# Revit family: ВПВО_Eng
name_source: partatom
category: Mechanical Equipment
units: mm (PartAtom-declared; Revit-internal decimal feet)

## family parameters
Always vertical = Yes
Classification = None
Cut with Voids When Loaded = No
Part Type = Normal
Room Calculation Point = No
Round Connector Dimension = Use Diameter
Shared = No
Work Plane-Based = No

## types (159) — shared parameters
00_20_Manufacturer = Vents
00_20_Name = Medium pressure axial fan
Casing Material = Metal, painted, blue, matte RAL 5007
Frequency = 50 Hz
Load Classification = HVAC
Maintenance zone material = <By Category>
Manufacturer = Vents
Number of Fase = 3
URL = https://ventilation-system.com
Voltage = 400 V
t = 5 mm  [stored 0.0164042 ft]
zero-valued in all types: Default Elevation

## per-type parameters (varying)
| type | D2 | D3 | Diameter | Dn | Dvu | Dy | L | Ld | Length | Lk1 | Lk2 | Lk3 | Ly | Maximum Air Flow | Power | Rk | Rk1 | Rn1 | Weight | t1 |
| VPVO-400-2D/0,55-6/25/PAG | 490 mm | 390 mm  [stored 1.27953 ft] | 490 mm | 404 mm  [stored 1.32546 ft] | 390 mm  [stored 1.27953 ft] | 400 mm  [stored 1.31234 ft] | 350 mm  [stored 1.14829 ft] | 250 mm  [stored 0.82021 ft] | 350 mm  [stored 1.14829 ft] | 170 mm  [stored 0.557743 ft] | 300 mm | 235 mm  [stored 0.770997 ft] | 175 mm  [stored 0.574147 ft] | 5220.0 m³/h | 550 W | 200 mm  [stored 0.656168 ft] | 215 mm | 207 mm  [stored 0.679134 ft] | 23.4 kg | 345 mm  [stored 1.13189 ft] |
| VPVO-400-2D/0,75-6/30/PAG | 490 mm | 390 mm  [stored 1.27953 ft] | 490 mm | 404 mm  [stored 1.32546 ft] | 390 mm  [stored 1.27953 ft] | 400 mm  [stored 1.31234 ft] | 350 mm  [stored 1.14829 ft] | 250 mm  [stored 0.82021 ft] | 350 mm  [stored 1.14829 ft] | 170 mm  [stored 0.557743 ft] | 300 mm | 235 mm  [stored 0.770997 ft] | 175 mm  [stored 0.574147 ft] | 6120.0 m³/h | 750 W | 200 mm  [stored 0.656168 ft] | 215 mm | 207 mm  [stored 0.679134 ft] | 26.5 kg | 345 mm  [stored 1.13189 ft] |
| VPVO-400-2D/1,1-6/35/PAG | 490 mm | 390 mm  [stored 1.27953 ft] | 490 mm | 404 mm  [stored 1.32546 ft] | 390 mm  [stored 1.27953 ft] | 400 mm  [stored 1.31234 ft] | 450 mm | 350 mm  [stored 1.14829 ft] | 450 mm | 270 mm  [stored 0.885827 ft] | 400 mm  [stored 1.31234 ft] | 335 mm  [stored 1.09908 ft] | 225 mm  [stored 0.738189 ft] | 7200.0 m³/h | 1100 W | 200 mm  [stored 0.656168 ft] | 215 mm | 207 mm  [stored 0.679134 ft] | 27 kg | 445 mm  [stored 1.45997 ft] |
| VPVO-400-2D/1,5-6/40/PAG | 490 mm | 390 mm  [stored 1.27953 ft] | 490 mm | 404 mm  [stored 1.32546 ft] | 390 mm  [stored 1.27953 ft] | 400 mm  [stored 1.31234 ft] | 450 mm | 350 mm  [stored 1.14829 ft] | 450 mm | 270 mm  [stored 0.885827 ft] | 400 mm  [stored 1.31234 ft] | 335 mm  [stored 1.09908 ft] | 225 mm  [stored 0.738189 ft] | 7740.0 m³/h | 1500 W | 200 mm  [stored 0.656168 ft] | 215 mm | 207 mm  [stored 0.679134 ft] | 32.5 kg | 445 mm  [stored 1.45997 ft] |
| VPVO-400-2D/2,2-6/45/PAG | 490 mm | 390 mm  [stored 1.27953 ft] | 490 mm | 404 mm  [stored 1.32546 ft] | 390 mm  [stored 1.27953 ft] | 400 mm  [stored 1.31234 ft] | 450 mm | 350 mm  [stored 1.14829 ft] | 450 mm | 270 mm  [stored 0.885827 ft] | 400 mm  [stored 1.31234 ft] | 335 mm  [stored 1.09908 ft] | 225 mm  [stored 0.738189 ft] | 8460.0 m³/h | 2200 W | 200 mm  [stored 0.656168 ft] | 215 mm | 207 mm  [stored 0.679134 ft] | 34.5 kg | 445 mm  [stored 1.45997 ft] |
| VPVO-400-2D/2,2-8/45/PAG | 490 mm | 390 mm  [stored 1.27953 ft] | 490 mm | 404 mm  [stored 1.32546 ft] | 390 mm  [stored 1.27953 ft] | 400 mm  [stored 1.31234 ft] | 450 mm | 350 mm  [stored 1.14829 ft] | 450 mm | 270 mm  [stored 0.885827 ft] | 400 mm  [stored 1.31234 ft] | 335 mm  [stored 1.09908 ft] | 225 mm  [stored 0.738189 ft] | 8820.0 m³/h | 2200 W | 200 mm  [stored 0.656168 ft] | 215 mm | 207 mm  [stored 0.679134 ft] | 35 kg | 445 mm  [stored 1.45997 ft] |
| VPVO-400-4D/0,12-6/30/PAG | 490 mm | 390 mm  [stored 1.27953 ft] | 490 mm | 404 mm  [stored 1.32546 ft] | 390 mm  [stored 1.27953 ft] | 400 mm  [stored 1.31234 ft] | 350 mm  [stored 1.14829 ft] | 250 mm  [stored 0.82021 ft] | 350 mm  [stored 1.14829 ft] | 170 mm  [stored 0.557743 ft] | 300 mm | 235 mm  [stored 0.770997 ft] | 175 mm  [stored 0.574147 ft] | 3168.0 m³/h | 120 W | 200 mm  [stored 0.656168 ft] | 215 mm | 207 mm  [stored 0.679134 ft] | 19.5 kg | 345 mm  [stored 1.13189 ft] |
| VPVO-400-4D/0,18-6/35/PAG | 490 mm | 390 mm  [stored 1.27953 ft] | 490 mm | 404 mm  [stored 1.32546 ft] | 390 mm  [stored 1.27953 ft] | 400 mm  [stored 1.31234 ft] | 350 mm  [stored 1.14829 ft] | 250 mm  [stored 0.82021 ft] | 350 mm  [stored 1.14829 ft] | 170 mm  [stored 0.557743 ft] | 300 mm | 235 mm  [stored 0.770997 ft] | 175 mm  [stored 0.574147 ft] | 3600.0 m³/h | 180 W | 200 mm  [stored 0.656168 ft] | 215 mm | 207 mm  [stored 0.679134 ft] | 19.8 kg | 345 mm  [stored 1.13189 ft] |
| VPVO-400-4D/0,18-6/40/PAG | 490 mm | 390 mm  [stored 1.27953 ft] | 490 mm | 404 mm  [stored 1.32546 ft] | 390 mm  [stored 1.27953 ft] | 400 mm  [stored 1.31234 ft] | 350 mm  [stored 1.14829 ft] | 250 mm  [stored 0.82021 ft] | 350 mm  [stored 1.14829 ft] | 170 mm  [stored 0.557743 ft] | 300 mm | 235 mm  [stored 0.770997 ft] | 175 mm  [stored 0.574147 ft] | 3780.0 m³/h | 180 W | 200 mm  [stored 0.656168 ft] | 215 mm | 207 mm  [stored 0.679134 ft] | 19.8 kg | 345 mm  [stored 1.13189 ft] |
| VPVO-400-4D/0,25-6/45/PAG | 490 mm | 390 mm  [stored 1.27953 ft] | 490 mm | 404 mm  [stored 1.32546 ft] | 390 mm  [stored 1.27953 ft] | 400 mm  [stored 1.31234 ft] | 350 mm  [stored 1.14829 ft] | 250 mm  [stored 0.82021 ft] | 350 mm  [stored 1.14829 ft] | 170 mm  [stored 0.557743 ft] | 300 mm | 235 mm  [stored 0.770997 ft] | 175 mm  [stored 0.574147 ft] | 4248.0 m³/h | 250 W | 200 mm  [stored 0.656168 ft] | 215 mm | 207 mm  [stored 0.679134 ft] | 23.2 kg | 345 mm  [stored 1.13189 ft] |
| VPVO-400-4D/0,37-8/45/PAG | 490 mm | 390 mm  [stored 1.27953 ft] | 490 mm | 404 mm  [stored 1.32546 ft] | 390 mm  [stored 1.27953 ft] | 400 mm  [stored 1.31234 ft] | 350 mm  [stored 1.14829 ft] | 250 mm  [stored 0.82021 ft] | 350 mm  [stored 1.14829 ft] | 170 mm  [stored 0.557743 ft] | 300 mm | 235 mm  [stored 0.770997 ft] | 175 mm  [stored 0.574147 ft] | 4320.0 m³/h | 370 W | 200 mm  [stored 0.656168 ft] | 215 mm | 207 mm  [stored 0.679134 ft] | 23.9 kg | 345 mm  [stored 1.13189 ft] |
| VPVO-450-2D/0,75-6/25/PAG | 540 mm | 440 mm  [stored 1.44357 ft] | 540 mm | 454 mm | 440 mm  [stored 1.44357 ft] | 450 mm | 350 mm  [stored 1.14829 ft] | 250 mm  [stored 0.82021 ft] | 350 mm  [stored 1.14829 ft] | 170 mm  [stored 0.557743 ft] | 300 mm | 235 mm  [stored 0.770997 ft] | 175 mm  [stored 0.574147 ft] | 6750.0 m³/h | 750 W | 225 mm  [stored 0.738189 ft] | 240 mm  [stored 0.787402 ft] | 232 mm  [stored 0.761155 ft] | 36.1 kg | 345 mm  [stored 1.13189 ft] |
| VPVO-450-2D/1,1-6/30/PAG | 540 mm | 440 mm  [stored 1.44357 ft] | 540 mm | 454 mm | 440 mm  [stored 1.44357 ft] | 450 mm | 450 mm | 350 mm  [stored 1.14829 ft] | 450 mm | 270 mm  [stored 0.885827 ft] | 400 mm  [stored 1.31234 ft] | 335 mm  [stored 1.09908 ft] | 225 mm  [stored 0.738189 ft] | 8280.0 m³/h | 1100 W | 225 mm  [stored 0.738189 ft] | 240 mm  [stored 0.787402 ft] | 232 mm  [stored 0.761155 ft] | 36.6 kg | 445 mm  [stored 1.45997 ft] |
| VPVO-450-2D/1,5-6/35/PAG | 540 mm | 440 mm  [stored 1.44357 ft] | 540 mm | 454 mm | 440 mm  [stored 1.44357 ft] | 450 mm | 450 mm | 350 mm  [stored 1.14829 ft] | 450 mm | 270 mm  [stored 0.885827 ft] | 400 mm  [stored 1.31234 ft] | 335 mm  [stored 1.09908 ft] | 225 mm  [stored 0.738189 ft] | 9720.0 m³/h | 1500 W | 225 mm  [stored 0.738189 ft] | 240 mm  [stored 0.787402 ft] | 232 mm  [stored 0.761155 ft] | 42.1 kg | 445 mm  [stored 1.45997 ft] |
| VPVO-450-2D/2,2-6/40/PAG | 540 mm | 440 mm  [stored 1.44357 ft] | 540 mm | 454 mm | 440 mm  [stored 1.44357 ft] | 450 mm | 450 mm | 350 mm  [stored 1.14829 ft] | 450 mm | 270 mm  [stored 0.885827 ft] | 400 mm  [stored 1.31234 ft] | 335 mm  [stored 1.09908 ft] | 225 mm  [stored 0.738189 ft] | 10800.0 m³/h | 2200 W | 225 mm  [stored 0.738189 ft] | 240 mm  [stored 0.787402 ft] | 232 mm  [stored 0.761155 ft] | 44.1 kg | 445 mm  [stored 1.45997 ft] |
| VPVO-450-2D/3-8/40/PAG | 540 mm | 440 mm  [stored 1.44357 ft] | 540 mm | 454 mm | 440 mm  [stored 1.44357 ft] | 450 mm | 450 mm | 350 mm  [stored 1.14829 ft] | 450 mm | 270 mm  [stored 0.885827 ft] | 400 mm  [stored 1.31234 ft] | 335 mm  [stored 1.09908 ft] | 225 mm  [stored 0.738189 ft] | 11250.0 m³/h | 3000 W | 225 mm  [stored 0.738189 ft] | 240 mm  [stored 0.787402 ft] | 232 mm  [stored 0.761155 ft] | 53.6 kg | 445 mm  [stored 1.45997 ft] |
| VPVO-450-2D/4-8/45/PAG | 540 mm | 440 mm  [stored 1.44357 ft] | 540 mm | 454 mm | 440 mm  [stored 1.44357 ft] | 450 mm | 550 mm | 450 mm | 550 mm | 370 mm  [stored 1.21391 ft] | 500 mm | 435 mm  [stored 1.42717 ft] | 275 mm | 12600.0 m³/h | 4000 W | 225 mm  [stored 0.738189 ft] | 240 mm  [stored 0.787402 ft] | 232 mm  [stored 0.761155 ft] | 63.7 kg | 545 mm |
| VPVO-450-4D/0,12-6/25/PAG | 540 mm | 440 mm  [stored 1.44357 ft] | 540 mm | 454 mm | 440 mm  [stored 1.44357 ft] | 450 mm | 350 mm  [stored 1.14829 ft] | 250 mm  [stored 0.82021 ft] | 350 mm  [stored 1.14829 ft] | 170 mm  [stored 0.557743 ft] | 300 mm | 235 mm  [stored 0.770997 ft] | 175 mm  [stored 0.574147 ft] | 3420.0 m³/h | 120 W | 225 mm  [stored 0.738189 ft] | 240 mm  [stored 0.787402 ft] | 232 mm  [stored 0.761155 ft] | 29.1 kg | 345 mm  [stored 1.13189 ft] |
| VPVO-450-4D/0,18-6/30/PAG | 540 mm | 440 mm  [stored 1.44357 ft] | 540 mm | 454 mm | 440 mm  [stored 1.44357 ft] | 450 mm | 350 mm  [stored 1.14829 ft] | 250 mm  [stored 0.82021 ft] | 350 mm  [stored 1.14829 ft] | 170 mm  [stored 0.557743 ft] | 300 mm | 235 mm  [stored 0.770997 ft] | 175 mm  [stored 0.574147 ft] | 3960.0 m³/h | 180 W | 225 mm  [stored 0.738189 ft] | 240 mm  [stored 0.787402 ft] | 232 mm  [stored 0.761155 ft] | 29.4 kg | 345 mm  [stored 1.13189 ft] |
| VPVO-450-4D/0,25-6/35/PAG | 540 mm | 440 mm  [stored 1.44357 ft] | 540 mm | 454 mm | 440 mm  [stored 1.44357 ft] | 450 mm | 350 mm  [stored 1.14829 ft] | 250 mm  [stored 0.82021 ft] | 350 mm  [stored 1.14829 ft] | 170 mm  [stored 0.557743 ft] | 300 mm | 235 mm  [stored 0.770997 ft] | 175 mm  [stored 0.574147 ft] | 4860.0 m³/h | 250 W | 225 mm  [stored 0.738189 ft] | 240 mm  [stored 0.787402 ft] | 232 mm  [stored 0.761155 ft] | 32.8 kg | 345 mm  [stored 1.13189 ft] |
| VPVO-450-4D/0,25-6/40/PAG | 540 mm | 440 mm  [stored 1.44357 ft] | 540 mm | 454 mm | 440 mm  [stored 1.44357 ft] | 450 mm | 350 mm  [stored 1.14829 ft] | 250 mm  [stored 0.82021 ft] | 350 mm  [stored 1.14829 ft] | 170 mm  [stored 0.557743 ft] | 300 mm | 235 mm  [stored 0.770997 ft] | 175 mm  [stored 0.574147 ft] | 5220.0 m³/h | 250 W | 225 mm  [stored 0.738189 ft] | 240 mm  [stored 0.787402 ft] | 232 mm  [stored 0.761155 ft] | 32.8 kg | 345 mm  [stored 1.13189 ft] |
| VPVO-450-4D/0,37-6/45/PAG | 540 mm | 440 mm  [stored 1.44357 ft] | 540 mm | 454 mm | 440 mm  [stored 1.44357 ft] | 450 mm | 350 mm  [stored 1.14829 ft] | 250 mm  [stored 0.82021 ft] | 350 mm  [stored 1.14829 ft] | 170 mm  [stored 0.557743 ft] | 300 mm | 235 mm  [stored 0.770997 ft] | 175 mm  [stored 0.574147 ft] | 5760.0 m³/h | 370 W | 225 mm  [stored 0.738189 ft] | 240 mm  [stored 0.787402 ft] | 232 mm  [stored 0.761155 ft] | 33 kg | 345 mm  [stored 1.13189 ft] |
| VPVO-450-4D/0,55-8/45/PAG | 540 mm | 440 mm  [stored 1.44357 ft] | 540 mm | 454 mm | 440 mm  [stored 1.44357 ft] | 450 mm | 350 mm  [stored 1.14829 ft] | 250 mm  [stored 0.82021 ft] | 350 mm  [stored 1.14829 ft] | 170 mm  [stored 0.557743 ft] | 300 mm | 235 mm  [stored 0.770997 ft] | 175 mm  [stored 0.574147 ft] | 6120.0 m³/h | 550 W | 225 mm  [stored 0.738189 ft] | 240 mm  [stored 0.787402 ft] | 232 mm  [stored 0.761155 ft] | 36.6 kg | 345 mm  [stored 1.13189 ft] |
| VPVO-500-2D/1,1-6/25/PAG | 600 mm | 490 mm | 600 mm | 504 mm | 490 mm | 500 mm | 450 mm | 350 mm  [stored 1.14829 ft] | 450 mm | 270 mm  [stored 0.885827 ft] | 400 mm  [stored 1.31234 ft] | 335 mm  [stored 1.09908 ft] | 225 mm  [stored 0.738189 ft] | 8460.0 m³/h | 1100 W | 250 mm  [stored 0.82021 ft] | 265 mm  [stored 0.869423 ft] | 257 mm  [stored 0.843176 ft] | 48.2 kg | 445 mm  [stored 1.45997 ft] |
| VPVO-560-2D/1,5-6/25/PAG | 660 mm | 550 mm | 660 mm | 564 mm | 550 mm | 560 mm | 450 mm | 350 mm  [stored 1.14829 ft] | 450 mm | 270 mm  [stored 0.885827 ft] | 400 mm  [stored 1.31234 ft] | 335 mm  [stored 1.09908 ft] | 225 mm  [stored 0.738189 ft] | 10440.0 m³/h | 1500 W | 280 mm  [stored 0.918635 ft] | 295 mm  [stored 0.967848 ft] | 287 mm | 70.8 kg | 445 mm  [stored 1.45997 ft] |
| VPVO-630-2D/3-8/25/PAG | 730 mm | 620 mm | 730 mm | 634 mm | 620 mm | 630 mm | 450 mm | 350 mm  [stored 1.14829 ft] | 450 mm | 270 mm  [stored 0.885827 ft] | 400 mm  [stored 1.31234 ft] | 335 mm  [stored 1.09908 ft] | 225 mm  [stored 0.738189 ft] | 13680.0 m³/h | 3000 W | 315 mm  [stored 1.03346 ft] | 330 mm  [stored 1.08268 ft] | 322 mm  [stored 1.05643 ft] | 88 kg | 445 mm  [stored 1.45997 ft] |
| VPVO-710-2D/7,5-6/20/PAG | 810 mm | 700 mm | 810 mm | 714 mm | 700 mm | 710 mm | 550 mm | 450 mm | 550 mm | 370 mm  [stored 1.21391 ft] | 500 mm | 435 mm  [stored 1.42717 ft] | 275 mm | 22680.0 m³/h | 7500 W | 355 mm | 370 mm  [stored 1.21391 ft] | 362 mm  [stored 1.18766 ft] | 150.8 kg | 545 mm |
| VPVO-800-4D/1,1-6/20/PAG | 900 mm | 790 mm | 900 mm | 804 mm | 790 mm | 800 mm | 450 mm | 350 mm  [stored 1.14829 ft] | 450 mm | 270 mm  [stored 0.885827 ft] | 400 mm  [stored 1.31234 ft] | 335 mm  [stored 1.09908 ft] | 225 mm  [stored 0.738189 ft] | 15120.0 m³/h | 1100 W | 400 mm  [stored 1.31234 ft] | 415 mm  [stored 1.36155 ft] | 407 mm  [stored 1.3353 ft] | 115.6 kg | 445 mm  [stored 1.45997 ft] |
| VPVO-900-4D/3-8/20/PAG | 1015 mm | 890 mm | 1015 mm | 904 mm | 890 mm | 900 mm | 550 mm | 450 mm | 550 mm | 370 mm  [stored 1.21391 ft] | 500 mm | 435 mm  [stored 1.42717 ft] | 275 mm | 21600.0 m³/h | 3000 W | 450 mm | 465 mm | 457 mm | 134.8 kg | 545 mm |
| VPVO-1000-4D/5,5-8/25/PAG | 1115 mm | 990 mm | 1115 mm | 1004 mm | 990 mm | 1000 mm | 550 mm | 450 mm | 550 mm | 370 mm  [stored 1.21391 ft] | 500 mm | 435 mm  [stored 1.42717 ft] | 275 mm | 30960.0 m³/h | 5500 W | 500 mm | 515 mm | 507 mm | 200.5 kg | 545 mm |
| VPVO-1120-4D/7,5-8/25/PAG | 1270 mm | 1110 mm | 1270 mm | 1124 mm | 1110 mm | 1120 mm | 650 mm | 550 mm | 650 mm | 470 mm | 600 mm | 535 mm | 325 mm  [stored 1.06627 ft] | 43920.0 m³/h | 7500 W | 560 mm | 575 mm | 567 mm | 222 kg | 645 mm |
| VPVO-1250-4D/7,5-8/25/PAG | 1400 mm | 1240 mm | 1400 mm | 1254 mm | 1240 mm | 1250 mm | 650 mm | 550 mm | 650 mm | 470 mm | 600 mm | 535 mm | 325 mm  [stored 1.06627 ft] | 45000.0 m³/h | 7500 W | 625 mm | 640 mm | 632 mm | 241 kg | 645 mm |
| VPVO-500-2D/1,5-6/30/PAG | 600 mm | 490 mm | 600 mm | 504 mm | 490 mm | 500 mm | 450 mm | 350 mm  [stored 1.14829 ft] | 450 mm | 270 mm  [stored 0.885827 ft] | 400 mm  [stored 1.31234 ft] | 335 mm  [stored 1.09908 ft] | 225 mm  [stored 0.738189 ft] | 10440.0 m³/h | 1500 W | 250 mm  [stored 0.82021 ft] | 265 mm  [stored 0.869423 ft] | 257 mm  [stored 0.843176 ft] | 53.7 kg | 445 mm  [stored 1.45997 ft] |
| VPVO-500-2D/2,2-6/35/PAG | 600 mm | 490 mm | 600 mm | 504 mm | 490 mm | 500 mm | 450 mm | 350 mm  [stored 1.14829 ft] | 450 mm | 270 mm  [stored 0.885827 ft] | 400 mm  [stored 1.31234 ft] | 335 mm  [stored 1.09908 ft] | 225 mm  [stored 0.738189 ft] | 12240.0 m³/h | 2200 W | 250 mm  [stored 0.82021 ft] | 265 mm  [stored 0.869423 ft] | 257 mm  [stored 0.843176 ft] | 55.7 kg | 445 mm  [stored 1.45997 ft] |
| VPVO-500-2D/3-8/35/PAG | 600 mm | 490 mm | 600 mm | 504 mm | 490 mm | 500 mm | 450 mm | 350 mm  [stored 1.14829 ft] | 450 mm | 270 mm  [stored 0.885827 ft] | 400 mm  [stored 1.31234 ft] | 335 mm  [stored 1.09908 ft] | 225 mm  [stored 0.738189 ft] | 13320.0 m³/h | 3000 W | 250 mm  [stored 0.82021 ft] | 265 mm  [stored 0.869423 ft] | 257 mm  [stored 0.843176 ft] | 65.3 kg | 445 mm  [stored 1.45997 ft] |
| VPVO-500-2D/4-8/40/PAG | 600 mm | 490 mm | 600 mm | 504 mm | 490 mm | 500 mm | 550 mm | 450 mm | 550 mm | 370 mm  [stored 1.21391 ft] | 500 mm | 435 mm  [stored 1.42717 ft] | 275 mm | 15120.0 m³/h | 4000 W | 250 mm  [stored 0.82021 ft] | 265 mm  [stored 0.869423 ft] | 257 mm  [stored 0.843176 ft] | 75.4 kg | 545 mm |
| VPVO-500-2D/5,5-8/45/PAG | 600 mm | 490 mm | 600 mm | 504 mm | 490 mm | 500 mm | 550 mm | 450 mm | 550 mm | 370 mm  [stored 1.21391 ft] | 500 mm | 435 mm  [stored 1.42717 ft] | 275 mm | 16200.0 m³/h | 5500 W | 250 mm  [stored 0.82021 ft] | 265 mm  [stored 0.869423 ft] | 257 mm  [stored 0.843176 ft] | 96.8 kg | 545 mm |
| VPVO-500-4D/0,18-6/25/PAG | 600 mm | 490 mm | 600 mm | 504 mm | 490 mm | 500 mm | 350 mm  [stored 1.14829 ft] | 250 mm  [stored 0.82021 ft] | 350 mm  [stored 1.14829 ft] | 170 mm  [stored 0.557743 ft] | 300 mm | 235 mm  [stored 0.770997 ft] | 175 mm  [stored 0.574147 ft] | 4320.0 m³/h | 180 W | 250 mm  [stored 0.82021 ft] | 265 mm  [stored 0.869423 ft] | 257 mm  [stored 0.843176 ft] | 61.5 kg | 345 mm  [stored 1.13189 ft] |
| VPVO-500-4D/0,25-6/30/PAG | 600 mm | 490 mm | 600 mm | 504 mm | 490 mm | 500 mm | 350 mm  [stored 1.14829 ft] | 250 mm  [stored 0.82021 ft] | 350 mm  [stored 1.14829 ft] | 170 mm  [stored 0.557743 ft] | 300 mm | 235 mm  [stored 0.770997 ft] | 175 mm  [stored 0.574147 ft] | 5256.0 m³/h | 250 W | 250 mm  [stored 0.82021 ft] | 265 mm  [stored 0.869423 ft] | 257 mm  [stored 0.843176 ft] | 61.7 kg | 345 mm  [stored 1.13189 ft] |
| VPVO-500-4D/0,37-6/35/PAG | 600 mm | 490 mm | 600 mm | 504 mm | 490 mm | 500 mm | 350 mm  [stored 1.14829 ft] | 250 mm  [stored 0.82021 ft] | 350 mm  [stored 1.14829 ft] | 170 mm  [stored 0.557743 ft] | 300 mm | 235 mm  [stored 0.770997 ft] | 175 mm  [stored 0.574147 ft] | 6120.0 m³/h | 370 W | 250 mm  [stored 0.82021 ft] | 265 mm  [stored 0.869423 ft] | 257 mm  [stored 0.843176 ft] | 64.8 kg | 345 mm  [stored 1.13189 ft] |
| VPVO-500-4D/0,37-6/40/PAG | 600 mm | 490 mm | 600 mm | 504 mm | 490 mm | 500 mm | 350 mm  [stored 1.14829 ft] | 250 mm  [stored 0.82021 ft] | 350 mm  [stored 1.14829 ft] | 170 mm  [stored 0.557743 ft] | 300 mm | 235 mm  [stored 0.770997 ft] | 175 mm  [stored 0.574147 ft] | 6480.0 m³/h | 370 W | 250 mm  [stored 0.82021 ft] | 265 mm  [stored 0.869423 ft] | 257 mm  [stored 0.843176 ft] | 64.8 kg | 345 mm  [stored 1.13189 ft] |
| VPVO-500-4D/0,55-6/45/PAG | 600 mm | 490 mm | 600 mm | 504 mm | 490 mm | 500 mm | 450 mm | 350 mm  [stored 1.14829 ft] | 450 mm | 270 mm  [stored 0.885827 ft] | 400 mm  [stored 1.31234 ft] | 335 mm  [stored 1.09908 ft] | 225 mm  [stored 0.738189 ft] | 7560.0 m³/h | 550 W | 250 mm  [stored 0.82021 ft] | 265 mm  [stored 0.869423 ft] | 257 mm  [stored 0.843176 ft] | 65.6 kg | 445 mm  [stored 1.45997 ft] |
| VPVO-500-4D/0,75-8/45/PAG | 600 mm | 490 mm | 600 mm | 504 mm | 490 mm | 500 mm | 450 mm | 350 mm  [stored 1.14829 ft] | 450 mm | 270 mm  [stored 0.885827 ft] | 400 mm  [stored 1.31234 ft] | 335 mm  [stored 1.09908 ft] | 225 mm  [stored 0.738189 ft] | 8280.0 m³/h | 750 W | 250 mm  [stored 0.82021 ft] | 265 mm  [stored 0.869423 ft] | 257 mm  [stored 0.843176 ft] | 71.4 kg | 445 mm  [stored 1.45997 ft] |
| VPVO-560-2D/2,2/6/30/PAG | 660 mm | 550 mm | 660 mm | 564 mm | 550 mm | 560 mm | 450 mm | 350 mm  [stored 1.14829 ft] | 450 mm | 270 mm  [stored 0.885827 ft] | 400 mm  [stored 1.31234 ft] | 335 mm  [stored 1.09908 ft] | 225 mm  [stored 0.738189 ft] | 12600.0 m³/h | 2200 W | 280 mm  [stored 0.918635 ft] | 295 mm  [stored 0.967848 ft] | 287 mm | 72.8 kg | 445 mm  [stored 1.45997 ft] |
| VPVO-560-2D/3-8/30/PAG | 660 mm | 550 mm | 660 mm | 564 mm | 550 mm | 560 mm | 450 mm | 350 mm  [stored 1.14829 ft] | 450 mm | 270 mm  [stored 0.885827 ft] | 400 mm  [stored 1.31234 ft] | 335 mm  [stored 1.09908 ft] | 225 mm  [stored 0.738189 ft] | 14040.0 m³/h | 3000 W | 280 mm  [stored 0.918635 ft] | 295 mm  [stored 0.967848 ft] | 287 mm | 82.4 kg | 445 mm  [stored 1.45997 ft] |
| VPVO-560-2D/4-8/35/PAG | 660 mm | 550 mm | 660 mm | 564 mm | 550 mm | 560 mm | 550 mm | 450 mm | 550 mm | 370 mm  [stored 1.21391 ft] | 500 mm | 435 mm  [stored 1.42717 ft] | 275 mm | 17280.0 m³/h | 4000 W | 280 mm  [stored 0.918635 ft] | 295 mm  [stored 0.967848 ft] | 287 mm | 92.5 kg | 545 mm |
| VPVO-560-2D/5,5-8/40/PAG | 660 mm | 550 mm | 660 mm | 564 mm | 550 mm | 560 mm | 550 mm | 450 mm | 550 mm | 370 mm  [stored 1.21391 ft] | 500 mm | 435 mm  [stored 1.42717 ft] | 275 mm | 18540.0 m³/h | 5500 W | 280 mm  [stored 0.918635 ft] | 295 mm  [stored 0.967848 ft] | 287 mm | 113.9 kg | 545 mm |
| VPVO-560-2D/7,5-8/45/PAG | 660 mm | 550 mm | 660 mm | 564 mm | 550 mm | 560 mm | 550 mm | 450 mm | 550 mm | 370 mm  [stored 1.21391 ft] | 500 mm | 435 mm  [stored 1.42717 ft] | 275 mm | 21600.0 m³/h | 7500 W | 280 mm  [stored 0.918635 ft] | 295 mm  [stored 0.967848 ft] | 287 mm | 117.9 kg | 545 mm |
| VPVO-560-4D/0,25-6/25/PAG | 660 mm | 550 mm | 660 mm | 564 mm | 550 mm | 560 mm | 350 mm  [stored 1.14829 ft] | 250 mm  [stored 0.82021 ft] | 350 mm  [stored 1.14829 ft] | 170 mm  [stored 0.557743 ft] | 300 mm | 235 mm  [stored 0.770997 ft] | 175 mm  [stored 0.574147 ft] | 5040.0 m³/h | 250 W | 280 mm  [stored 0.918635 ft] | 295 mm  [stored 0.967848 ft] | 287 mm | 61.5 kg | 345 mm  [stored 1.13189 ft] |
| VPVO-560-4D/0,37-6/30/PAG | 660 mm | 550 mm | 660 mm | 564 mm | 550 mm | 560 mm | 350 mm  [stored 1.14829 ft] | 250 mm  [stored 0.82021 ft] | 350 mm  [stored 1.14829 ft] | 170 mm  [stored 0.557743 ft] | 300 mm | 235 mm  [stored 0.770997 ft] | 175 mm  [stored 0.574147 ft] | 6480.0 m³/h | 370 W | 280 mm  [stored 0.918635 ft] | 295 mm  [stored 0.967848 ft] | 287 mm | 61.7 kg | 345 mm  [stored 1.13189 ft] |
| VPVO-560-4D/0,55-6/35/PAG | 660 mm | 550 mm | 660 mm | 564 mm | 550 mm | 560 mm | 350 mm  [stored 1.14829 ft] | 250 mm  [stored 0.82021 ft] | 350 mm  [stored 1.14829 ft] | 170 mm  [stored 0.557743 ft] | 300 mm | 235 mm  [stored 0.770997 ft] | 175 mm  [stored 0.574147 ft] | 7740.0 m³/h | 550 W | 280 mm  [stored 0.918635 ft] | 295 mm  [stored 0.967848 ft] | 287 mm | 64.8 kg | 345 mm  [stored 1.13189 ft] |
| VPVO-560-4D/0,55-6/40/PAG | 660 mm | 550 mm | 660 mm | 564 mm | 550 mm | 560 mm | 350 mm  [stored 1.14829 ft] | 250 mm  [stored 0.82021 ft] | 350 mm  [stored 1.14829 ft] | 170 mm  [stored 0.557743 ft] | 300 mm | 235 mm  [stored 0.770997 ft] | 175 mm  [stored 0.574147 ft] | 8640.0 m³/h | 550 W | 280 mm  [stored 0.918635 ft] | 295 mm  [stored 0.967848 ft] | 287 mm | 64.8 kg | 345 mm  [stored 1.13189 ft] |
| VPVO-560-4D/0,75-6/45/PAG | 660 mm | 550 mm | 660 mm | 564 mm | 550 mm | 560 mm | 450 mm | 350 mm  [stored 1.14829 ft] | 450 mm | 270 mm  [stored 0.885827 ft] | 400 mm  [stored 1.31234 ft] | 335 mm  [stored 1.09908 ft] | 225 mm  [stored 0.738189 ft] | 9360.0 m³/h | 750 W | 280 mm  [stored 0.918635 ft] | 295 mm  [stored 0.967848 ft] | 287 mm | 65.6 kg | 445 mm  [stored 1.45997 ft] |
| VPVO-560-4D/1,1-8/45/PAG | 660 mm | 550 mm | 660 mm | 564 mm | 550 mm | 560 mm | 450 mm | 350 mm  [stored 1.14829 ft] | 450 mm | 270 mm  [stored 0.885827 ft] | 400 mm  [stored 1.31234 ft] | 335 mm  [stored 1.09908 ft] | 225 mm  [stored 0.738189 ft] | 10800.0 m³/h | 1100 W | 280 mm  [stored 0.918635 ft] | 295 mm  [stored 0.967848 ft] | 287 mm | 71.4 kg | 445 mm  [stored 1.45997 ft] |
| VPVO-630-2D/4-8/30/PAG | 730 mm | 620 mm | 730 mm | 634 mm | 620 mm | 630 mm | 550 mm | 450 mm | 550 mm | 370 mm  [stored 1.21391 ft] | 500 mm | 435 mm  [stored 1.42717 ft] | 275 mm | 16920.0 m³/h | 4000 W | 315 mm  [stored 1.03346 ft] | 330 mm  [stored 1.08268 ft] | 322 mm  [stored 1.05643 ft] | 98.1 kg | 545 mm |
| VPVO-630-2D/5,5-8/35/PAG | 730 mm | 620 mm | 730 mm | 634 mm | 620 mm | 630 mm | 550 mm | 450 mm | 550 mm | 370 mm  [stored 1.21391 ft] | 500 mm | 435 mm  [stored 1.42717 ft] | 275 mm | 21600.0 m³/h | 5500 W | 315 mm  [stored 1.03346 ft] | 330 mm  [stored 1.08268 ft] | 322 mm  [stored 1.05643 ft] | 119.5 kg | 545 mm |
| VPVO-630-2D/7,5-8/40/PAG | 730 mm | 620 mm | 730 mm | 634 mm | 620 mm | 630 mm | 550 mm | 450 mm | 550 mm | 370 mm  [stored 1.21391 ft] | 500 mm | 435 mm  [stored 1.42717 ft] | 275 mm | 24480.0 m³/h | 7500 W | 315 mm  [stored 1.03346 ft] | 330 mm  [stored 1.08268 ft] | 322 mm  [stored 1.05643 ft] | 123.5 kg | 545 mm |
| VPVO-630-2D/9,2-6/30/PAG | 730 mm | 620 mm | 730 mm | 634 mm | 620 mm | 630 mm | 650 mm | 550 mm | 650 mm | 470 mm | 600 mm | 535 mm | 325 mm  [stored 1.06627 ft] | 25920.0 m³/h | 9200 W | 315 mm  [stored 1.03346 ft] | 330 mm  [stored 1.08268 ft] | 322 mm  [stored 1.05643 ft] | 130.1 kg | 645 mm |
| VPVO-630-2D/11-6/32,5/PAG | 730 mm | 620 mm | 730 mm | 634 mm | 620 mm | 630 mm | 650 mm | 550 mm | 650 mm | 470 mm | 600 mm | 535 mm | 325 mm  [stored 1.06627 ft] | 27000.0 m³/h | 11000 W | 315 mm  [stored 1.03346 ft] | 330 mm  [stored 1.08268 ft] | 322 mm  [stored 1.05643 ft] | 154.1 kg | 645 mm |
| VPVO-630-2D/11-6/35/PAG | 730 mm | 620 mm | 730 mm | 634 mm | 620 mm | 630 mm | 650 mm | 550 mm | 650 mm | 470 mm | 600 mm | 535 mm | 325 mm  [stored 1.06627 ft] | 29880.0 m³/h | 11000 W | 315 mm  [stored 1.03346 ft] | 330 mm  [stored 1.08268 ft] | 322 mm  [stored 1.05643 ft] | 154.1 kg | 645 mm |
| VPVO-630-2D/15-6/37,5/PAG | 730 mm | 620 mm | 730 mm | 634 mm | 620 mm | 630 mm | 750 mm | 650 mm | 750 mm | 570 mm | 700 mm | 635 mm | 375 mm  [stored 1.23031 ft] | 30240.0 m³/h | 15000 W | 315 mm  [stored 1.03346 ft] | 330 mm  [stored 1.08268 ft] | 322 mm  [stored 1.05643 ft] | 166.7 kg | 745 mm |
| VPVO-630-2D/15-6/40/PAG | 730 mm | 620 mm | 730 mm | 634 mm | 620 mm | 630 mm | 750 mm | 650 mm | 750 mm | 570 mm | 700 mm | 635 mm | 375 mm  [stored 1.23031 ft] | 31140.0 m³/h | 15000 W | 315 mm  [stored 1.03346 ft] | 330 mm  [stored 1.08268 ft] | 322 mm  [stored 1.05643 ft] | 166.7 kg | 745 mm |
| VPVO-630-2D/18,5-6/45/PAG | 730 mm | 620 mm | 730 mm | 634 mm | 620 mm | 630 mm | 750 mm | 650 mm | 750 mm | 570 mm | 700 mm | 635 mm | 375 mm  [stored 1.23031 ft] | 33840.0 m³/h | 18500 W | 315 mm  [stored 1.03346 ft] | 330 mm  [stored 1.08268 ft] | 322 mm  [stored 1.05643 ft] | 179.8 kg | 745 mm |
| VPVO-630-4D/0,37-8/25/PAG | 730 mm | 620 mm | 730 mm | 634 mm | 620 mm | 630 mm | 350 mm  [stored 1.14829 ft] | 250 mm  [stored 0.82021 ft] | 350 mm  [stored 1.14829 ft] | 170 mm  [stored 0.557743 ft] | 300 mm | 235 mm  [stored 0.770997 ft] | 175 mm  [stored 0.574147 ft] | 6840.0 m³/h | 370 W | 315 mm  [stored 1.03346 ft] | 330 mm  [stored 1.08268 ft] | 322 mm  [stored 1.05643 ft] | 67.9 kg | 345 mm  [stored 1.13189 ft] |
| VPVO-630-4D/0,55-8/30/PAG | 730 mm | 620 mm | 730 mm | 634 mm | 620 mm | 630 mm | 350 mm  [stored 1.14829 ft] | 250 mm  [stored 0.82021 ft] | 350 mm  [stored 1.14829 ft] | 170 mm  [stored 0.557743 ft] | 300 mm | 235 mm  [stored 0.770997 ft] | 175 mm  [stored 0.574147 ft] | 9000.0 m³/h | 550 W | 315 mm  [stored 1.03346 ft] | 330 mm  [stored 1.08268 ft] | 322 mm  [stored 1.05643 ft] | 71 kg | 345 mm  [stored 1.13189 ft] |
| VPVO-630-4D/0,75-8/35/PAG | 730 mm | 620 mm | 730 mm | 634 mm | 620 mm | 630 mm | 450 mm | 350 mm  [stored 1.14829 ft] | 450 mm | 270 mm  [stored 0.885827 ft] | 400 mm  [stored 1.31234 ft] | 335 mm  [stored 1.09908 ft] | 225 mm  [stored 0.738189 ft] | 10440.0 m³/h | 750 W | 315 mm  [stored 1.03346 ft] | 330 mm  [stored 1.08268 ft] | 322 mm  [stored 1.05643 ft] | 71.8 kg | 445 mm  [stored 1.45997 ft] |
| VPVO-630-4D/1,1-8/40/PAG | 730 mm | 620 mm | 730 mm | 634 mm | 620 mm | 630 mm | 450 mm | 350 mm  [stored 1.14829 ft] | 450 mm | 270 mm  [stored 0.885827 ft] | 400 mm  [stored 1.31234 ft] | 335 mm  [stored 1.09908 ft] | 225 mm  [stored 0.738189 ft] | 12240.0 m³/h | 1100 W | 315 mm  [stored 1.03346 ft] | 330 mm  [stored 1.08268 ft] | 322 mm  [stored 1.05643 ft] | 77 kg | 445 mm  [stored 1.45997 ft] |
| VPVO-630-4D/1,5-6/32,5/PAG | 730 mm | 620 mm | 730 mm | 634 mm | 620 mm | 630 mm | 450 mm | 350 mm  [stored 1.14829 ft] | 450 mm | 270 mm  [stored 0.885827 ft] | 400 mm  [stored 1.31234 ft] | 335 mm  [stored 1.09908 ft] | 225 mm  [stored 0.738189 ft] | 14040.0 m³/h | 1500 W | 315 mm  [stored 1.03346 ft] | 330 mm  [stored 1.08268 ft] | 322 mm  [stored 1.05643 ft] | 81.1 kg | 445 mm  [stored 1.45997 ft] |
| VPVO-630-4D/1,5-8/45/PAG | 730 mm | 620 mm | 730 mm | 634 mm | 620 mm | 630 mm | 450 mm | 350 mm  [stored 1.14829 ft] | 450 mm | 270 mm  [stored 0.885827 ft] | 400 mm  [stored 1.31234 ft] | 335 mm  [stored 1.09908 ft] | 225 mm  [stored 0.738189 ft] | 14400.0 m³/h | 1500 W | 315 mm  [stored 1.03346 ft] | 330 mm  [stored 1.08268 ft] | 322 mm  [stored 1.05643 ft] | 80 kg | 445 mm  [stored 1.45997 ft] |
| VPVO-630-4D/1,5-6/37,5/PAG | 730 mm | 620 mm | 730 mm | 634 mm | 620 mm | 630 mm | 450 mm | 350 mm  [stored 1.14829 ft] | 450 mm | 270 mm  [stored 0.885827 ft] | 400 mm  [stored 1.31234 ft] | 335 mm  [stored 1.09908 ft] | 225 mm  [stored 0.738189 ft] | 14940.0 m³/h | 1500 W | 315 mm  [stored 1.03346 ft] | 330 mm  [stored 1.08268 ft] | 322 mm  [stored 1.05643 ft] | 81.1 kg | 445 mm  [stored 1.45997 ft] |
| VPVO-630-4D/2,2-6/40/PAG | 730 mm | 620 mm | 730 mm | 634 mm | 620 mm | 630 mm | 450 mm | 350 mm  [stored 1.14829 ft] | 450 mm | 270 mm  [stored 0.885827 ft] | 400 mm  [stored 1.31234 ft] | 335 mm  [stored 1.09908 ft] | 225 mm  [stored 0.738189 ft] | 15480.0 m³/h | 2200 W | 315 mm  [stored 1.03346 ft] | 330 mm  [stored 1.08268 ft] | 322 mm  [stored 1.05643 ft] | 83.2 kg | 445 mm  [stored 1.45997 ft] |
| VPVO-630-4D/2,2-6/45/PAG | 730 mm | 620 mm | 730 mm | 634 mm | 620 mm | 630 mm | 450 mm | 350 mm  [stored 1.14829 ft] | 450 mm | 270 mm  [stored 0.885827 ft] | 400 mm  [stored 1.31234 ft] | 335 mm  [stored 1.09908 ft] | 225 mm  [stored 0.738189 ft] | 16920.0 m³/h | 2200 W | 315 mm  [stored 1.03346 ft] | 330 mm  [stored 1.08268 ft] | 322 mm  [stored 1.05643 ft] | 83.2 kg | 445 mm  [stored 1.45997 ft] |
| VPVO-710-2D/9,2-6/25/PAG | 810 mm | 700 mm | 810 mm | 714 mm | 700 mm | 710 mm | 650 mm | 550 mm | 650 mm | 470 mm | 600 mm | 535 mm | 325 mm  [stored 1.06627 ft] | 28440.0 m³/h | 9200 W | 355 mm | 370 mm  [stored 1.21391 ft] | 362 mm  [stored 1.18766 ft] | 156.3 kg | 645 mm |
| VPVO-710-2D/15-6/30/PAG | 810 mm | 700 mm | 810 mm | 714 mm | 700 mm | 710 mm | 750 mm | 650 mm | 750 mm | 570 mm | 700 mm | 635 mm | 375 mm  [stored 1.23031 ft] | 33840.0 m³/h | 15000 W | 355 mm | 370 mm  [stored 1.21391 ft] | 362 mm  [stored 1.18766 ft] | 192.9 kg | 745 mm |
| VPVO-710-2D/15-6/32,5/PAG | 810 mm | 700 mm | 810 mm | 714 mm | 700 mm | 710 mm | 750 mm | 650 mm | 750 mm | 570 mm | 700 mm | 635 mm | 375 mm  [stored 1.23031 ft] | 37440.0 m³/h | 15000 W | 355 mm | 370 mm  [stored 1.21391 ft] | 362 mm  [stored 1.18766 ft] | 192.9 kg | 745 mm |
| VPVO-710-2D/18,5-6/35/PAG | 810 mm | 700 mm | 810 mm | 714 mm | 700 mm | 710 mm | 750 mm | 650 mm | 750 mm | 570 mm | 700 mm | 635 mm | 375 mm  [stored 1.23031 ft] | 38880.0 m³/h | 18500 W | 355 mm | 370 mm  [stored 1.21391 ft] | 362 mm  [stored 1.18766 ft] | 206 kg | 745 mm |
| VPVO-710-2D/18,5-6/37,5/PAG | 810 mm | 700 mm | 810 mm | 714 mm | 700 mm | 710 mm | 750 mm | 650 mm | 750 mm | 570 mm | 700 mm | 635 mm | 375 mm  [stored 1.23031 ft] | 41040.0 m³/h | 18500 W | 355 mm | 370 mm  [stored 1.21391 ft] | 362 mm  [stored 1.18766 ft] | 206 kg | 745 mm |
| VPVO-710-2D/22-6/40/PAG | 810 mm | 700 mm | 810 mm | 714 mm | 700 mm | 710 mm | 850 mm | 750 mm | 850 mm | 670 mm | 800 mm | 735 mm | 425 mm  [stored 1.39436 ft] | 43200.0 m³/h | 22000 W | 355 mm | 370 mm  [stored 1.21391 ft] | 362 mm  [stored 1.18766 ft] | 246 kg | 845 mm |
| VPVO-710-4D/0,75-6/20/PAG | 810 mm | 700 mm | 810 mm | 714 mm | 700 mm | 710 mm | 450 mm | 350 mm  [stored 1.14829 ft] | 450 mm | 270 mm  [stored 0.885827 ft] | 400 mm  [stored 1.31234 ft] | 335 mm  [stored 1.09908 ft] | 225 mm  [stored 0.738189 ft] | 11520.0 m³/h | 750 W | 355 mm | 370 mm  [stored 1.21391 ft] | 362 mm  [stored 1.18766 ft] | 99.1 kg | 445 mm  [stored 1.45997 ft] |
| VPVO-710-4D/1,1-6/25/PAG | 810 mm | 700 mm | 810 mm | 714 mm | 700 mm | 710 mm | 450 mm | 350 mm  [stored 1.14829 ft] | 450 mm | 270 mm  [stored 0.885827 ft] | 400 mm  [stored 1.31234 ft] | 335 mm  [stored 1.09908 ft] | 225 mm  [stored 0.738189 ft] | 14400.0 m³/h | 1100 W | 355 mm | 370 mm  [stored 1.21391 ft] | 362 mm  [stored 1.18766 ft] | 104.3 kg | 445 mm  [stored 1.45997 ft] |
| VPVO-710-4D/1,5-6/30/PAG | 810 mm | 700 mm | 810 mm | 714 mm | 700 mm | 710 mm | 450 mm | 350 mm  [stored 1.14829 ft] | 450 mm | 270 mm  [stored 0.885827 ft] | 400 mm  [stored 1.31234 ft] | 335 mm  [stored 1.09908 ft] | 225 mm  [stored 0.738189 ft] | 16920.0 m³/h | 1500 W | 355 mm | 370 mm  [stored 1.21391 ft] | 362 mm  [stored 1.18766 ft] | 107.3 kg | 445 mm  [stored 1.45997 ft] |
| VPVO-710-4D/2,2-6/32,5/PAG | 810 mm | 700 mm | 810 mm | 714 mm | 700 mm | 710 mm | 450 mm | 350 mm  [stored 1.14829 ft] | 450 mm | 270 mm  [stored 0.885827 ft] | 400 mm  [stored 1.31234 ft] | 335 mm  [stored 1.09908 ft] | 225 mm  [stored 0.738189 ft] | 19080.0 m³/h | 2200 W | 355 mm | 370 mm  [stored 1.21391 ft] | 362 mm  [stored 1.18766 ft] | 109.4 kg | 445 mm  [stored 1.45997 ft] |
| VPVO-710-4D/2,2-6/35/PAG | 810 mm | 700 mm | 810 mm | 714 mm | 700 mm | 710 mm | 450 mm | 350 mm  [stored 1.14829 ft] | 450 mm | 270 mm  [stored 0.885827 ft] | 400 mm  [stored 1.31234 ft] | 335 mm  [stored 1.09908 ft] | 225 mm  [stored 0.738189 ft] | 19800.0 m³/h | 2200 W | 355 mm | 370 mm  [stored 1.21391 ft] | 362 mm  [stored 1.18766 ft] | 109.4 kg | 445 mm  [stored 1.45997 ft] |
| VPVO-710-4D/2,2-6/37,5/PAG | 810 mm | 700 mm | 810 mm | 714 mm | 700 mm | 710 mm | 450 mm | 350 mm  [stored 1.14829 ft] | 450 mm | 270 mm  [stored 0.885827 ft] | 400 mm  [stored 1.31234 ft] | 335 mm  [stored 1.09908 ft] | 225 mm  [stored 0.738189 ft] | 20520.0 m³/h | 2200 W | 355 mm | 370 mm  [stored 1.21391 ft] | 362 mm  [stored 1.18766 ft] | 109.4 kg | 445 mm  [stored 1.45997 ft] |
| VPVO-710-4D/3-6/40/PAG | 810 mm | 700 mm | 810 mm | 714 mm | 700 mm | 710 mm | 550 mm | 450 mm | 550 mm | 370 mm  [stored 1.21391 ft] | 500 mm | 435 mm  [stored 1.42717 ft] | 275 mm | 21240.0 m³/h | 3000 W | 355 mm | 370 mm  [stored 1.21391 ft] | 362 mm  [stored 1.18766 ft] | 118.3 kg | 545 mm |
| VPVO-710-4D/4-6/45/PAG | 810 mm | 700 mm | 810 mm | 714 mm | 700 mm | 710 mm | 550 mm | 450 mm | 550 mm | 370 mm  [stored 1.21391 ft] | 500 mm | 435 mm  [stored 1.42717 ft] | 275 mm | 21240.0 m³/h | 6400 W | 355 mm | 370 mm  [stored 1.21391 ft] | 362 mm  [stored 1.18766 ft] | 129.4 kg | 545 mm |
| VPVO-800-4D/1,5-6/25/PAG | 900 mm | 790 mm | 900 mm | 804 mm | 790 mm | 800 mm | 450 mm | 350 mm  [stored 1.14829 ft] | 450 mm | 270 mm  [stored 0.885827 ft] | 400 mm  [stored 1.31234 ft] | 335 mm  [stored 1.09908 ft] | 225 mm  [stored 0.738189 ft] | 18360.0 m³/h | 1500 W | 400 mm  [stored 1.31234 ft] | 415 mm  [stored 1.36155 ft] | 407 mm  [stored 1.3353 ft] | 118.6 kg | 445 mm  [stored 1.45997 ft] |
| VPVO-800-4D/2,2-6/30/PAG | 900 mm | 790 mm | 900 mm | 804 mm | 790 mm | 800 mm | 450 mm | 350 mm  [stored 1.14829 ft] | 450 mm | 270 mm  [stored 0.885827 ft] | 400 mm  [stored 1.31234 ft] | 335 mm  [stored 1.09908 ft] | 225 mm  [stored 0.738189 ft] | 21060.0 m³/h | 2200 W | 400 mm  [stored 1.31234 ft] | 415 mm  [stored 1.36155 ft] | 407 mm  [stored 1.3353 ft] | 120.7 kg | 445 mm  [stored 1.45997 ft] |
| VPVO-800-4D/3-6/32,5/PAG | 900 mm | 790 mm | 900 mm | 804 mm | 790 mm | 800 mm | 550 mm | 450 mm | 550 mm | 370 mm  [stored 1.21391 ft] | 500 mm | 435 mm  [stored 1.42717 ft] | 275 mm | 24480.0 m³/h | 3000 W | 400 mm  [stored 1.31234 ft] | 415 mm  [stored 1.36155 ft] | 407 mm  [stored 1.3353 ft] | 129.6 kg | 545 mm |
| VPVO-800-4D/3-6/35/PAG | 900 mm | 790 mm | 900 mm | 804 mm | 790 mm | 800 mm | 550 mm | 450 mm | 550 mm | 370 mm  [stored 1.21391 ft] | 500 mm | 435 mm  [stored 1.42717 ft] | 275 mm | 26640.0 m³/h | 3000 W | 400 mm  [stored 1.31234 ft] | 415 mm  [stored 1.36155 ft] | 407 mm  [stored 1.3353 ft] | 129.6 kg | 545 mm |
| VPVO-800-4D/4-6/37,5/PAG | 900 mm | 790 mm | 900 mm | 804 mm | 790 mm | 800 mm | 550 mm | 450 mm | 550 mm | 370 mm  [stored 1.21391 ft] | 500 mm | 435 mm  [stored 1.42717 ft] | 275 mm | 27000.0 m³/h | 4000 W | 400 mm  [stored 1.31234 ft] | 415 mm  [stored 1.36155 ft] | 407 mm  [stored 1.3353 ft] | 140.7 kg | 545 mm |
| VPVO-800-4D/4-6/40/PAG | 900 mm | 790 mm | 900 mm | 804 mm | 790 mm | 800 mm | 550 mm | 450 mm | 550 mm | 370 mm  [stored 1.21391 ft] | 500 mm | 435 mm  [stored 1.42717 ft] | 275 mm | 28980.0 m³/h | 4000 W | 400 mm  [stored 1.31234 ft] | 415 mm  [stored 1.36155 ft] | 407 mm  [stored 1.3353 ft] | 140.7 kg | 545 mm |
| VPVO-800-4D/5,5-6/45/PAG | 900 mm | 790 mm | 900 mm | 804 mm | 790 mm | 800 mm | 550 mm | 450 mm | 550 mm | 370 mm  [stored 1.21391 ft] | 500 mm | 435 mm  [stored 1.42717 ft] | 275 mm | 31320.0 m³/h | 5500 W | 400 mm  [stored 1.31234 ft] | 415 mm  [stored 1.36155 ft] | 407 mm  [stored 1.3353 ft] | 157.6 kg | 545 mm |
| VPVO-800-6D/0,37-6/20/PAG | 900 mm | 790 mm | 900 mm | 804 mm | 790 mm | 800 mm | 450 mm | 350 mm  [stored 1.14829 ft] | 450 mm | 270 mm  [stored 0.885827 ft] | 400 mm  [stored 1.31234 ft] | 335 mm  [stored 1.09908 ft] | 225 mm  [stored 0.738189 ft] | 9720.0 m³/h | 370 W | 400 mm  [stored 1.31234 ft] | 415 mm  [stored 1.36155 ft] | 407 mm  [stored 1.3353 ft] | 109.6 kg | 445 mm  [stored 1.45997 ft] |
| VPVO-800-6D/0,55-6/25/PAG | 900 mm | 790 mm | 900 mm | 804 mm | 790 mm | 800 mm | 450 mm | 350 mm  [stored 1.14829 ft] | 450 mm | 270 mm  [stored 0.885827 ft] | 400 mm  [stored 1.31234 ft] | 335 mm  [stored 1.09908 ft] | 225 mm  [stored 0.738189 ft] | 12960.0 m³/h | 550 W | 400 mm  [stored 1.31234 ft] | 415 mm  [stored 1.36155 ft] | 407 mm  [stored 1.3353 ft] | 111.1 kg | 445 mm  [stored 1.45997 ft] |
| VPVO-800-6D/0,75-6/30/PAG | 900 mm | 790 mm | 900 mm | 804 mm | 790 mm | 800 mm | 450 mm | 350 mm  [stored 1.14829 ft] | 450 mm | 270 mm  [stored 0.885827 ft] | 400 mm  [stored 1.31234 ft] | 335 mm  [stored 1.09908 ft] | 225 mm  [stored 0.738189 ft] | 15120.0 m³/h | 750 W | 400 mm  [stored 1.31234 ft] | 415 mm  [stored 1.36155 ft] | 407 mm  [stored 1.3353 ft] | 116.4 kg | 445 mm  [stored 1.45997 ft] |
| VPVO-800-6D/0,75-6/32,5/PAG | 900 mm | 790 mm | 900 mm | 804 mm | 790 mm | 800 mm | 450 mm | 350 mm  [stored 1.14829 ft] | 450 mm | 270 mm  [stored 0.885827 ft] | 400 mm  [stored 1.31234 ft] | 335 mm  [stored 1.09908 ft] | 225 mm  [stored 0.738189 ft] | 15840.0 m³/h | 750 W | 400 mm  [stored 1.31234 ft] | 415 mm  [stored 1.36155 ft] | 407 mm  [stored 1.3353 ft] | 116.4 kg | 445 mm  [stored 1.45997 ft] |
| VPVO-800-6D/1,1-6/35/PAG | 900 mm | 790 mm | 900 mm | 804 mm | 790 mm | 800 mm | 450 mm | 350 mm  [stored 1.14829 ft] | 450 mm | 270 mm  [stored 0.885827 ft] | 400 mm  [stored 1.31234 ft] | 335 mm  [stored 1.09908 ft] | 225 mm  [stored 0.738189 ft] | 18000.0 m³/h | 1100 W | 400 mm  [stored 1.31234 ft] | 415 mm  [stored 1.36155 ft] | 407 mm  [stored 1.3353 ft] | 116.5 kg | 445 mm  [stored 1.45997 ft] |
| VPVO-800-6D/1,1-6/37,5/PAG | 900 mm | 790 mm | 900 mm | 804 mm | 790 mm | 800 mm | 450 mm | 350 mm  [stored 1.14829 ft] | 450 mm | 270 mm  [stored 0.885827 ft] | 400 mm  [stored 1.31234 ft] | 335 mm  [stored 1.09908 ft] | 225 mm  [stored 0.738189 ft] | 18720.0 m³/h | 1100 W | 400 mm  [stored 1.31234 ft] | 415 mm  [stored 1.36155 ft] | 407 mm  [stored 1.3353 ft] | 116.5 kg | 445 mm  [stored 1.45997 ft] |
| VPVO-800-6D/1,1-6/40/PAG | 900 mm | 790 mm | 900 mm | 804 mm | 790 mm | 800 mm | 450 mm | 350 mm  [stored 1.14829 ft] | 450 mm | 270 mm  [stored 0.885827 ft] | 400 mm  [stored 1.31234 ft] | 335 mm  [stored 1.09908 ft] | 225 mm  [stored 0.738189 ft] | 19440.0 m³/h | 1100 W | 400 mm  [stored 1.31234 ft] | 415 mm  [stored 1.36155 ft] | 407 mm  [stored 1.3353 ft] | 116.5 kg | 445 mm  [stored 1.45997 ft] |
| VPVO-800-6D/1,5-6/45/PAG | 900 mm | 790 mm | 900 mm | 804 mm | 790 mm | 800 mm | 550 mm | 450 mm | 550 mm | 370 mm  [stored 1.21391 ft] | 500 mm | 435 mm  [stored 1.42717 ft] | 275 mm | 20520.0 m³/h | 1500 W | 400 mm  [stored 1.31234 ft] | 415 mm  [stored 1.36155 ft] | 407 mm  [stored 1.3353 ft] | 124.6 kg | 545 mm |
| VPVO-900-4D/4-8/25/PAG | 1015 mm | 890 mm | 1015 mm | 904 mm | 890 mm | 900 mm | 550 mm | 450 mm | 550 mm | 370 mm  [stored 1.21391 ft] | 500 mm | 435 mm  [stored 1.42717 ft] | 275 mm | 26280.0 m³/h | 4000 W | 450 mm | 465 mm | 457 mm | 145.9 kg | 545 mm |
| VPVO-900-4D/5,5-8/30/PAG | 1015 mm | 890 mm | 1015 mm | 904 mm | 890 mm | 900 mm | 550 mm | 450 mm | 550 mm | 370 mm  [stored 1.21391 ft] | 500 mm | 435 mm  [stored 1.42717 ft] | 275 mm | 31680.0 m³/h | 5500 W | 450 mm | 465 mm | 457 mm | 162.8 kg | 545 mm |
| VPVO-900-4D/5,5-8/32,5/PAG | 1015 mm | 890 mm | 1015 mm | 904 mm | 890 mm | 900 mm | 550 mm | 450 mm | 550 mm | 370 mm  [stored 1.21391 ft] | 500 mm | 435 mm  [stored 1.42717 ft] | 275 mm | 32400.0 m³/h | 5500 W | 450 mm | 465 mm | 457 mm | 162.8 kg | 545 mm |
| VPVO-900-4D/7,5-8/35/PAG | 1015 mm | 890 mm | 1015 mm | 904 mm | 890 mm | 900 mm | 650 mm | 550 mm | 650 mm | 470 mm | 600 mm | 535 mm | 325 mm  [stored 1.06627 ft] | 34920.0 m³/h | 7500 W | 450 mm | 465 mm | 457 mm | 165.3 kg | 645 mm |
| VPVO-900-4D/7,5-8/37,5/PAG | 1015 mm | 890 mm | 1015 mm | 904 mm | 890 mm | 900 mm | 650 mm | 550 mm | 650 mm | 470 mm | 600 mm | 535 mm | 325 mm  [stored 1.06627 ft] | 37440.0 m³/h | 7500 W | 450 mm | 465 mm | 457 mm | 165.3 kg | 645 mm |
| VPVO-900-4D/7,5-8/40/PAG | 1015 mm | 890 mm | 1015 mm | 904 mm | 890 mm | 900 mm | 650 mm | 550 mm | 650 mm | 470 mm | 600 mm | 535 mm | 325 mm  [stored 1.06627 ft] | 38520.0 m³/h | 7500 W | 450 mm | 465 mm | 457 mm | 165.3 kg | 645 mm |
| VPVO-900-4D/11-8/45/PAG | 1015 mm | 890 mm | 1015 mm | 904 mm | 890 mm | 900 mm | 750 mm | 650 mm | 750 mm | 570 mm | 700 mm | 635 mm | 375 mm  [stored 1.23031 ft] | 43200.0 m³/h | 11000 W | 450 mm | 465 mm | 457 mm | 199.6 kg | 745 mm |
| VPVO-900-6D/0,75-8/20/PAG | 1015 mm | 890 mm | 1015 mm | 904 mm | 890 mm | 900 mm | 450 mm | 350 mm  [stored 1.14829 ft] | 450 mm | 270 mm  [stored 0.885827 ft] | 400 mm  [stored 1.31234 ft] | 335 mm  [stored 1.09908 ft] | 225 mm  [stored 0.738189 ft] | 14040.0 m³/h | 750 W | 450 mm | 465 mm | 457 mm | 121.6 kg | 445 mm  [stored 1.45997 ft] |
| VPVO-900-6D/1,1-8/25/PAG | 1015 mm | 890 mm | 1015 mm | 904 mm | 890 mm | 900 mm | 450 mm | 350 mm  [stored 1.14829 ft] | 450 mm | 270 mm  [stored 0.885827 ft] | 400 mm  [stored 1.31234 ft] | 335 mm  [stored 1.09908 ft] | 225 mm  [stored 0.738189 ft] | 16920.0 m³/h | 1100 W | 450 mm | 465 mm | 457 mm | 121.7 kg | 445 mm  [stored 1.45997 ft] |
| VPVO-900-6D/1,5-8/30/PAG | 1015 mm | 890 mm | 1015 mm | 904 mm | 890 mm | 900 mm | 550 mm | 450 mm | 550 mm | 370 mm  [stored 1.21391 ft] | 500 mm | 435 mm  [stored 1.42717 ft] | 275 mm | 20520.0 m³/h | 1500 W | 450 mm | 465 mm | 457 mm | 129.8 kg | 545 mm |
| VPVO-900-6D/1,5-8/32,5/PAG | 1015 mm | 890 mm | 1015 mm | 904 mm | 890 mm | 900 mm | 550 mm | 450 mm | 550 mm | 370 mm  [stored 1.21391 ft] | 500 mm | 435 mm  [stored 1.42717 ft] | 275 mm | 21240.0 m³/h | 1500 W | 450 mm | 465 mm | 457 mm | 129.8 kg | 545 mm |
| VPVO-900-6D/2,2-8/35/PAG | 1015 mm | 890 mm | 1015 mm | 904 mm | 890 mm | 900 mm | 550 mm | 450 mm | 550 mm | 370 mm  [stored 1.21391 ft] | 500 mm | 435 mm  [stored 1.42717 ft] | 275 mm | 24120.0 m³/h | 2200 W | 450 mm | 465 mm | 457 mm | 135.3 kg | 545 mm |
| VPVO-900-6D/2,2-8/37,5/PAG | 1015 mm | 890 mm | 1015 mm | 904 mm | 890 mm | 900 mm | 550 mm | 450 mm | 550 mm | 370 mm  [stored 1.21391 ft] | 500 mm | 435 mm  [stored 1.42717 ft] | 275 mm | 25200.0 m³/h | 2200 W | 450 mm | 465 mm | 457 mm | 135.3 kg | 545 mm |
| VPVO-900-6D/2,2-8/40/PAG | 1015 mm | 890 mm | 1015 mm | 904 mm | 890 mm | 900 mm | 550 mm | 450 mm | 550 mm | 370 mm  [stored 1.21391 ft] | 500 mm | 435 mm  [stored 1.42717 ft] | 275 mm | 25560.0 m³/h | 2200 W | 450 mm | 465 mm | 457 mm | 135.3 kg | 545 mm |
| VPVO-900-6D/3-8/45/PAG | 1015 mm | 890 mm | 1015 mm | 904 mm | 890 mm | 900 mm | 650 mm | 550 mm | 650 mm | 470 mm | 600 mm | 535 mm | 325 mm  [stored 1.06627 ft] | 28980.0 m³/h | 3000 W | 450 mm | 465 mm | 457 mm | 155.8 kg | 645 mm |
| VPVO-1000-4D/7,5-8/30/PAG | 1115 mm | 990 mm | 1115 mm | 1004 mm | 990 mm | 1000 mm | 650 mm | 550 mm | 650 mm | 470 mm | 600 mm | 535 mm | 325 mm  [stored 1.06627 ft] | 38520.0 m³/h | 7500 W | 500 mm | 515 mm | 507 mm | 203 kg | 645 mm |
| VPVO-1000-4D/7,5-8/32,5/PAG | 1115 mm | 990 mm | 1115 mm | 1004 mm | 990 mm | 1000 mm | 650 mm | 550 mm | 650 mm | 470 mm | 600 mm | 535 mm | 325 mm  [stored 1.06627 ft] | 43200.0 m³/h | 7500 W | 500 mm | 515 mm | 507 mm | 203 kg | 645 mm |
| VPVO-1000-4D/9,2-8/35/PAG | 1115 mm | 990 mm | 1115 mm | 1004 mm | 990 mm | 1000 mm | 650 mm | 550 mm | 650 mm | 470 mm | 600 mm | 535 mm | 325 mm  [stored 1.06627 ft] | 46080.0 m³/h | 9200 W | 500 mm | 515 mm | 507 mm | 233.5 kg | 645 mm |
| VPVO-1000-4D/11-8/37,5/PAG | 1115 mm | 990 mm | 1115 mm | 1004 mm | 990 mm | 1000 mm | 800 mm | 700 mm | 800 mm | 620 mm | 750 mm | 685 mm | 400 mm  [stored 1.31234 ft] | 50040.0 m³/h | 11000 W | 500 mm | 515 mm | 507 mm | 237.3 kg | 795 mm |
| VPVO-1000-4D/11-8/40/PAG | 1115 mm | 990 mm | 1115 mm | 1004 mm | 990 mm | 1000 mm | 800 mm | 700 mm | 800 mm | 620 mm | 750 mm | 685 mm | 400 mm  [stored 1.31234 ft] | 52200.0 m³/h | 11000 W | 500 mm | 515 mm | 507 mm | 237.3 kg | 795 mm |
| VPVO-1000-4D/15-8/45/PAG | 1115 mm | 990 mm | 1115 mm | 1004 mm | 990 mm | 1000 mm | 800 mm | 700 mm | 800 mm | 620 mm | 750 mm | 685 mm | 400 mm  [stored 1.31234 ft] | 56880.0 m³/h | 15000 W | 500 mm | 515 mm | 507 mm | 256.4 kg | 795 mm |
| VPVO-1000-4D/18,5-8/50/PAG | 1115 mm | 990 mm | 1115 mm | 1004 mm | 990 mm | 1000 mm | 900 mm | 800 mm | 900 mm | 720 mm | 850 mm | 785 mm | 450 mm | 61920.0 m³/h | 18500 W | 500 mm | 515 mm | 507 mm | 301.9 kg | 895 mm |
| VPVO-1000-6D/1,5-8/25/PAG | 1115 mm | 990 mm | 1115 mm | 1004 mm | 990 mm | 1000 mm | 550 mm | 450 mm | 550 mm | 370 mm  [stored 1.21391 ft] | 500 mm | 435 mm  [stored 1.42717 ft] | 275 mm | 20880.0 m³/h | 1500 W | 500 mm | 515 mm | 507 mm | 167.5 kg | 545 mm |
| VPVO-1000-6D/2,2-8/30/PAG | 1115 mm | 990 mm | 1115 mm | 1004 mm | 990 mm | 1000 mm | 550 mm | 450 mm | 550 mm | 370 mm  [stored 1.21391 ft] | 500 mm | 435 mm  [stored 1.42717 ft] | 275 mm | 25920.0 m³/h | 2200 W | 500 mm | 515 mm | 507 mm | 173 kg | 545 mm |
| VPVO-1000-6D/2,2-8/32,5/PAG | 1115 mm | 990 mm | 1115 mm | 1004 mm | 990 mm | 1000 mm | 550 mm | 450 mm | 550 mm | 370 mm  [stored 1.21391 ft] | 500 mm | 435 mm  [stored 1.42717 ft] | 275 mm | 27720.0 m³/h | 2200 W | 500 mm | 515 mm | 507 mm | 173 kg | 545 mm |
| VPVO-1000-6D/3-8/35/PAG | 1115 mm | 990 mm | 1115 mm | 1004 mm | 990 mm | 1000 mm | 650 mm | 550 mm | 650 mm | 470 mm | 600 mm | 535 mm | 325 mm  [stored 1.06627 ft] | 31140.0 m³/h | 3000 W | 500 mm | 515 mm | 507 mm | 193.5 kg | 645 mm |
| VPVO-1000-6D/3-8/37,5/PAG | 1115 mm | 990 mm | 1115 mm | 1004 mm | 990 mm | 1000 mm | 650 mm | 550 mm | 650 mm | 470 mm | 600 mm | 535 mm | 325 mm  [stored 1.06627 ft] | 32400.0 m³/h | 3000 W | 500 mm | 515 mm | 507 mm | 193.5 kg | 645 mm |
| VPVO-1000-6D/4-8/40/PAG | 1115 mm | 990 mm | 1115 mm | 1004 mm | 990 mm | 1000 mm | 650 mm | 550 mm | 650 mm | 470 mm | 600 mm | 535 mm | 325 mm  [stored 1.06627 ft] | 34920.0 m³/h | 4000 W | 500 mm | 515 mm | 507 mm | 203.5 kg | 645 mm |
| VPVO-1000-6D/5,5-8/45/PAG | 1115 mm | 990 mm | 1115 mm | 1004 mm | 990 mm | 1000 mm | 650 mm | 550 mm | 650 mm | 470 mm | 600 mm | 535 mm | 325 mm  [stored 1.06627 ft] | 37440.0 m³/h | 5500 W | 500 mm | 515 mm | 507 mm | 207.5 kg | 645 mm |
| VPVO-1000-6D/5,5-8/50/PAG | 1115 mm | 990 mm | 1115 mm | 1004 mm | 990 mm | 1000 mm | 650 mm | 550 mm | 650 mm | 470 mm | 600 mm | 535 mm | 325 mm  [stored 1.06627 ft] | 41760.0 m³/h | 5500 W | 500 mm | 515 mm | 507 mm | 207.5 kg | 645 mm |
| VPVO-1120-4D/11-8/30/PAG | 1270 mm | 1110 mm | 1270 mm | 1124 mm | 1110 mm | 1120 mm | 800 mm | 700 mm | 800 mm | 620 mm | 750 mm | 685 mm | 400 mm  [stored 1.31234 ft] | 54720.0 m³/h | 11000 W | 560 mm | 575 mm | 567 mm | 256.3 kg | 795 mm |
| VPVO-1120-4D/11-8/32,5/PAG | 1270 mm | 1110 mm | 1270 mm | 1124 mm | 1110 mm | 1120 mm | 800 mm | 700 mm | 800 mm | 620 mm | 750 mm | 685 mm | 400 mm  [stored 1.31234 ft] | 59400.0 m³/h | 11000 W | 560 mm | 575 mm | 567 mm | 256.3 kg | 795 mm |
| VPVO-1120-4D/15-8/35/PAG | 1270 mm | 1110 mm | 1270 mm | 1124 mm | 1110 mm | 1120 mm | 800 mm | 700 mm | 800 mm | 620 mm | 750 mm | 685 mm | 400 mm  [stored 1.31234 ft] | 64800.0 m³/h | 15000 W | 560 mm | 575 mm | 567 mm | 275.4 kg | 795 mm |
| VPVO-1120-4D/18,5-8/37,5/PAG | 1270 mm | 1110 mm | 1270 mm | 1124 mm | 1110 mm | 1120 mm | 900 mm | 800 mm | 900 mm | 720 mm | 850 mm | 785 mm | 450 mm | 69120.0 m³/h | 18500 W | 560 mm | 575 mm | 567 mm | 320.9 kg | 895 mm |
| VPVO-1120-4D/18,5-8/40/PAG | 1270 mm | 1110 mm | 1270 mm | 1124 mm | 1110 mm | 1120 mm | 900 mm | 800 mm | 900 mm | 720 mm | 850 mm | 785 mm | 450 mm | 73800.0 m³/h | 18500 W | 560 mm | 575 mm | 567 mm | 320.9 kg | 895 mm |
| VPVO-1120-4D/22-8/45/PAG | 1270 mm | 1110 mm | 1270 mm | 1124 mm | 1110 mm | 1120 mm | 900 mm | 800 mm | 900 mm | 720 mm | 850 mm | 785 mm | 450 mm | 79920.0 m³/h | 22000 W | 560 mm | 575 mm | 567 mm | 334.2 kg | 895 mm |
| VPVO-1120-6D/2,2-8/25/PAG | 1270 mm | 1110 mm | 1270 mm | 1124 mm | 1110 mm | 1120 mm | 550 mm | 450 mm | 550 mm | 370 mm  [stored 1.21391 ft] | 500 mm | 435 mm  [stored 1.42717 ft] | 275 mm | 29880.0 m³/h | 2200 W | 560 mm | 575 mm | 567 mm | 192 kg | 545 mm |
| VPVO-1120-6D/3-8/30/PAG | 1270 mm | 1110 mm | 1270 mm | 1124 mm | 1110 mm | 1120 mm | 650 mm | 550 mm | 650 mm | 470 mm | 600 mm | 535 mm | 325 mm  [stored 1.06627 ft] | 36000.0 m³/h | 3000 W | 560 mm | 575 mm | 567 mm | 212.5 kg | 645 mm |
| VPVO-1120-6D/4-8/32,5/PAG | 1270 mm | 1110 mm | 1270 mm | 1124 mm | 1110 mm | 1120 mm | 650 mm | 550 mm | 650 mm | 470 mm | 600 mm | 535 mm | 325 mm  [stored 1.06627 ft] | 41040.0 m³/h | 4000 W | 560 mm | 575 mm | 567 mm | 222.5 kg | 645 mm |
| VPVO-1120-6D/4-8/35/PAG | 1270 mm | 1110 mm | 1270 mm | 1124 mm | 1110 mm | 1120 mm | 650 mm | 550 mm | 650 mm | 470 mm | 600 mm | 535 mm | 325 mm  [stored 1.06627 ft] | 43200.0 m³/h | 4000 W | 560 mm | 575 mm | 567 mm | 222.5 kg | 645 mm |
| VPVO-1120-6D/5,5-8/37,5/PAG | 1270 mm | 1110 mm | 1270 mm | 1124 mm | 1110 mm | 1120 mm | 650 mm | 550 mm | 650 mm | 470 mm | 600 mm | 535 mm | 325 mm  [stored 1.06627 ft] | 46080.0 m³/h | 5500 W | 560 mm | 575 mm | 567 mm | 226.5 kg | 645 mm |
| VPVO-1120-6D/5,5-8/40/PAG | 1270 mm | 1110 mm | 1270 mm | 1124 mm | 1110 mm | 1120 mm | 650 mm | 550 mm | 650 mm | 470 mm | 600 mm | 535 mm | 325 mm  [stored 1.06627 ft] | 50040.0 m³/h | 5500 W | 560 mm | 575 mm | 567 mm | 226.5 kg | 645 mm |
| VPVO-1120-6D/7,5-8/45/PAG | 1270 mm | 1110 mm | 1270 mm | 1124 mm | 1110 mm | 1120 mm | 800 mm | 700 mm | 800 mm | 620 mm | 750 mm | 685 mm | 400 mm  [stored 1.31234 ft] | 52920.0 m³/h | 7500 W | 560 mm | 575 mm | 567 mm | 254.8 kg | 795 mm |
| VPVO-1120-6D/9,2-8/50/PAG | 1270 mm | 1110 mm | 1270 mm | 1124 mm | 1110 mm | 1120 mm | 800 mm | 700 mm | 800 mm | 620 mm | 750 mm | 685 mm | 400 mm  [stored 1.31234 ft] | 59040.0 m³/h | 9200 W | 560 mm | 575 mm | 567 mm | 272.5 kg | 795 mm |
| VPVO-1250-4D/11-8/30/PAG | 1400 mm | 1240 mm | 1400 mm | 1254 mm | 1240 mm | 1250 mm | 800 mm | 700 mm | 800 mm | 620 mm | 750 mm | 685 mm | 400 mm  [stored 1.31234 ft] | 63720.0 m³/h | 11000 W | 625 mm | 640 mm | 632 mm | 275.3 kg | 795 mm |
| VPVO-1250-4D/15-8/32,5/PAG | 1400 mm | 1240 mm | 1400 mm | 1254 mm | 1240 mm | 1250 mm | 800 mm | 700 mm | 800 mm | 620 mm | 750 mm | 685 mm | 400 mm  [stored 1.31234 ft] | 69840.0 m³/h | 15000 W | 625 mm | 640 mm | 632 mm | 294.4 kg | 795 mm |
| VPVO-1250-4D/15-8/35/PAG | 1400 mm | 1240 mm | 1400 mm | 1254 mm | 1240 mm | 1250 mm | 800 mm | 700 mm | 800 mm | 620 mm | 750 mm | 685 mm | 400 mm  [stored 1.31234 ft] | 75960.0 m³/h | 15000 W | 625 mm | 640 mm | 632 mm | 294.4 kg | 795 mm |
| VPVO-1250-4D/18,5-8/37,5/PAG | 1400 mm | 1240 mm | 1400 mm | 1254 mm | 1240 mm | 1250 mm | 900 mm | 800 mm | 900 mm | 720 mm | 850 mm | 785 mm | 450 mm | 83880.0 m³/h | 18500 W | 625 mm | 640 mm | 632 mm | 339.9 kg | 895 mm |
| VPVO-1250-4D/22-8/40/PAG | 1400 mm | 1240 mm | 1400 mm | 1254 mm | 1240 mm | 1250 mm | 900 mm | 800 mm | 900 mm | 720 mm | 850 mm | 785 mm | 450 mm | 90000.0 m³/h | 22000 W | 625 mm | 640 mm | 632 mm | 353.2 kg | 895 mm |
| VPVO-1250-4D/30-8/45/PAG | 1400 mm | 1240 mm | 1400 mm | 1254 mm | 1240 mm | 1250 mm | 900 mm | 800 mm | 900 mm | 720 mm | 850 mm | 785 mm | 450 mm | 100080.0 m³/h | 30000 W | 625 mm | 640 mm | 632 mm | 416.2 kg | 895 mm |
| VPVO-1250-6D/2,2-8/25/PAG | 1400 mm | 1240 mm | 1400 mm | 1254 mm | 1240 mm | 1250 mm | 550 mm | 450 mm | 550 mm | 370 mm  [stored 1.21391 ft] | 500 mm | 435 mm  [stored 1.42717 ft] | 275 mm | 31500.0 m³/h | 2200 W | 625 mm | 640 mm | 632 mm | 211 kg | 545 mm |
| VPVO-1250-6D/3-8/30/PAG | 1400 mm | 1240 mm | 1400 mm | 1254 mm | 1240 mm | 1250 mm | 650 mm | 550 mm | 650 mm | 470 mm | 600 mm | 535 mm | 325 mm  [stored 1.06627 ft] | 41400.0 m³/h | 3000 W | 625 mm | 640 mm | 632 mm | 231.5 kg | 645 mm |
| VPVO-1250-6D/4-8/32,5/PAG | 1400 mm | 1240 mm | 1400 mm | 1254 mm | 1240 mm | 1250 mm | 650 mm | 550 mm | 650 mm | 470 mm | 600 mm | 535 mm | 325 mm  [stored 1.06627 ft] | 46080.0 m³/h | 4000 W | 625 mm | 640 mm | 632 mm | 241.5 kg | 645 mm |
| VPVO-1250-6D/5,5-8/35/PAG | 1400 mm | 1240 mm | 1400 mm | 1254 mm | 1240 mm | 1250 mm | 650 mm | 550 mm | 650 mm | 470 mm | 600 mm | 535 mm | 325 mm  [stored 1.06627 ft] | 50400.0 m³/h | 5500 W | 625 mm | 640 mm | 632 mm | 245.5 kg | 645 mm |
| VPVO-1250-6D/5,5-8/37,5/PAG | 1400 mm | 1240 mm | 1400 mm | 1254 mm | 1240 mm | 1250 mm | 650 mm | 550 mm | 650 mm | 470 mm | 600 mm | 535 mm | 325 mm  [stored 1.06627 ft] | 56160.0 m³/h | 5500 W | 625 mm | 640 mm | 632 mm | 245.5 kg | 645 mm |
| VPVO-1250-6D/7,5-8/40/PAG | 1400 mm | 1240 mm | 1400 mm | 1254 mm | 1240 mm | 1250 mm | 800 mm | 700 mm | 800 mm | 620 mm | 750 mm | 685 mm | 400 mm  [stored 1.31234 ft] | 57600.0 m³/h | 7500 W | 625 mm | 640 mm | 632 mm | 273.8 kg | 795 mm |
| VPVO-1250-6D/9,2-8/45/PAG | 1400 mm | 1240 mm | 1400 mm | 1254 mm | 1240 mm | 1250 mm | 800 mm | 700 mm | 800 mm | 620 mm | 750 mm | 685 mm | 400 mm  [stored 1.31234 ft] | 66960.0 m³/h | 9200 W | 625 mm | 640 mm | 632 mm | 291.5 kg | 795 mm |
| VPVO-1250-6D/11-8/50/PAG | 1400 mm | 1240 mm | 1400 mm | 1254 mm | 1240 mm | 1250 mm | 800 mm | 700 mm | 800 mm | 620 mm | 750 mm | 685 mm | 400 mm  [stored 1.31234 ft] | 68940.0 m³/h | 11000 W | 625 mm | 640 mm | 632 mm | 299.3 kg | 795 mm |

note: column(s) folded — value = type name in every type: 00_20_Type

note: [stored X ft] marks values corroborated as IEEE doubles in the binary element streams (Revit-internal decimal feet)
